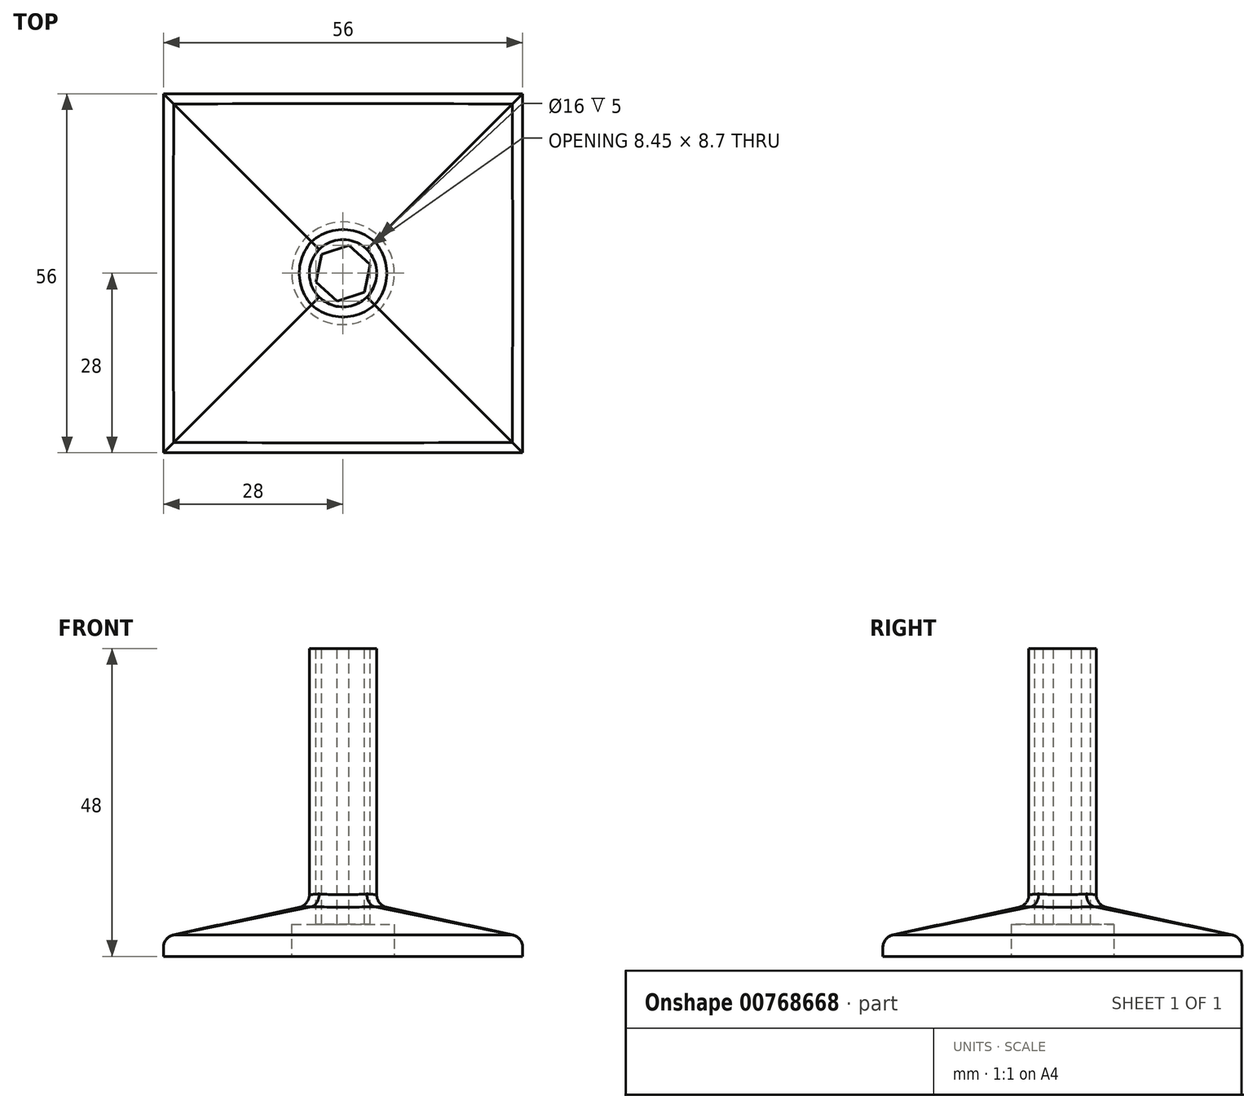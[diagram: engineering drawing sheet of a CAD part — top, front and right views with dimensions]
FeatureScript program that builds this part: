
annotation { "Feature Type Name" : "Feature", "Feature Type Description" : "" }
export const myFeature = defineFeature(function(context is Context, id is Id, definition is map)
    precondition{}
    {
        {
            var Q0;
            Q0=qCreatedBy(makeId("Top.planeOp"),FACE);
            cPlane(context, id + "F0", {"entities" : qUnion([Q0]), "cplaneType" : CPlaneType.OFFSET, "offset" : 8 * mm, "width" : 150 * mm, "height" : 150 * mm});
        }
        {
            var Q0;
            Q0=qCreatedBy(makeId("Top.planeOp"),FACE);
            var sketch = newSketch(context, id + "F1", { "sketchPlane" : qUnion([Q0])});
            skLineSegment(sketch, "E0.bottom", {"start": v(-28, 28) * mm, "end": v(28, 28) * mm});
            skLineSegment(sketch, "E0.top", {"start": v(-28, -28) * mm, "end": v(28, -28) * mm});
            skLineSegment(sketch, "E0.left", {"start": v(-28, 28) * mm, "end": v(-28, -28) * mm});
            skLineSegment(sketch, "E0.right", {"start": v(28, 28) * mm, "end": v(28, -28) * mm});
            skSolve(sketch);
        }
        {
            var Q0;
            Q0=makeQuery(id+"F1.imprint","IMPRINT",FACE,{"disambiguationData":[TD([[makeQuery(id+"F1.imprint","IMPRINT",EDGE,{"derivedFrom":sQuery(id+"F1.wireOp",EDGE,"E0.bottom")}),-1.0]])]});
            extrude(context, id + "F2", {"entities" : qUnion([Q0]), "depth" : 3 * mm, "offsetDistance" : 25 * mm});
        }
        {
            var Q0;
            Q0=qCreatedBy(id+"F0.planeOp",FACE);
            var sketch = newSketch(context, id + "F3", { "sketchPlane" : qUnion([Q0])});
            skCircle(sketch, "E1", {"center": v(0, 0) * mm, "radius": 5.25 * mm});
            skSolve(sketch);
        }
        {
            var Q0;
            Q0=makeQuery(id+"F3.imprint","IMPRINT",FACE,{"disambiguationData":[TD([[makeQuery(id+"F3.imprint","IMPRINT",EDGE,{"derivedFrom":sQuery(id+"F3.wireOp",EDGE,"E1")}),1.0]])]});
            extrude(context, id + "F4", {"entities" : qUnion([Q0]), "operationType" : NewBodyOperationType.ADD, "depth" : 40 * mm, "offsetDistance" : 25 * mm});
        }
        {
            var Q0;
            Q0=makeQuery(id+"F3.imprint","IMPRINT",FACE,{"disambiguationData":[TD([[makeQuery(id+"F3.imprint","IMPRINT",EDGE,{"derivedFrom":sQuery(id+"F3.wireOp",EDGE,"E1")}),1.0]])]});
            var Q1;
            Q1=makeQuery(id+"F2.opExtrude","CAP_FACE",FACE,{"disambiguationData":[OSD([sQuery(id+"F1.wireOp",EDGE,"E0.bottom"),sQuery(id+"F1.wireOp",EDGE,"E0.top"),sQuery(id+"F1.wireOp",EDGE,"E0.left"),sQuery(id+"F1.wireOp",EDGE,"E0.right")])],"isStart":false});
            loft(context, id + "F5", {"sheetProfilesArray" : [{ "sheetProfileEntities" : qUnion([Q0]) }, { "sheetProfileEntities" : qUnion([Q1]) }]});
        }
        {
            var Q0;
            Q0=makeQuery(id+"F2.opExtrude","CAP_FACE",FACE,{"disambiguationData":[OSD([sQuery(id+"F1.wireOp",EDGE,"E0.bottom"),sQuery(id+"F1.wireOp",EDGE,"E0.top"),sQuery(id+"F1.wireOp",EDGE,"E0.left"),sQuery(id+"F1.wireOp",EDGE,"E0.right")])],"isStart":true});
            var sketch = newSketch(context, id + "F6", { "sketchPlane" : qUnion([Q0])});
            skCircle(sketch, "E2", {"center": v(0, 0) * mm, "radius": 8 * mm});
            skSolve(sketch);
        }
        {
            var Q0;
            Q0=makeQuery(id+"F4.opExtrude","CAP_FACE",FACE,{"disambiguationData":[OSD([sQuery(id+"F3.wireOp",EDGE,"E1")])],"isStart":false});
            var sketch = newSketch(context, id + "F7", { "sketchPlane" : qUnion([Q0])});
            skCircle(sketch, "E3.cCircle", {"center": v(0, 0) * mm, "radius": 3.85 * mm, "construction": true});
            skLineSegment(sketch, "E3.0", {"start": v(4.23, 1.38) * mm, "end": v(3.3, -2.97) * mm});
            skLineSegment(sketch, "E3.1", {"start": v(3.3, -2.97) * mm, "end": v(-0.92, -4.35) * mm});
            skLineSegment(sketch, "E3.2", {"start": v(-0.92, -4.35) * mm, "end": v(-4.23, -1.38) * mm});
            skLineSegment(sketch, "E3.3", {"start": v(-4.23, -1.38) * mm, "end": v(-3.3, 2.97) * mm});
            skLineSegment(sketch, "E3.4", {"start": v(-3.3, 2.97) * mm, "end": v(0.92, 4.35) * mm});
            skLineSegment(sketch, "E3.5", {"start": v(0.92, 4.35) * mm, "end": v(4.23, 1.38) * mm});
            skPoint(sketch, "E3.0.midPoint", {"position": v(3.77, -0.8) * mm});
            skSolve(sketch);
        }
        {
            var Q0;
            Q0 = qSketchRegion(id + "F6", true);
            extrude(context, id + "F8", {"entities" : qUnion([Q0]), "operationType" : NewBodyOperationType.REMOVE, "oppositeDirection" : true, "depth" : 5 * mm, "offsetDistance" : 25 * mm});
        }
        {
            var Q0;
            Q0=makeQuery(id+"F7.imprint","IMPRINT",FACE,{"disambiguationData":[TD([[makeQuery(id+"F7.imprint","IMPRINT",EDGE,{"derivedFrom":sQuery(id+"F7.wireOp",EDGE,"E3.0")}),-1.0]])]});
            var Q1;
            Q1=makeQuery(id+"F2.opExtrude","CAP_FACE",FACE,{"disambiguationData":[OSD([sQuery(id+"F1.wireOp",EDGE,"E0.bottom"),sQuery(id+"F1.wireOp",EDGE,"E0.top"),sQuery(id+"F1.wireOp",EDGE,"E0.left"),sQuery(id+"F1.wireOp",EDGE,"E0.right")])],"isStart":true});
            extrude(context, id + "F9", {"entities" : qUnion([Q0]), "operationType" : NewBodyOperationType.REMOVE, "endBound" : BoundingType.THROUGH_ALL, "oppositeDirection" : true, "depth" : 25 * mm, "endBoundEntityFace" : qUnion([Q1]), "offsetDistance" : 25 * mm});
        }
        {
            var Q0;
            Q0=makeQuery(id+"F4.opExtrude","SWEPT_BODY",BODY,{"disambiguationData":[OSD([sQuery(id+"F3.wireOp",EDGE,"E1")])]});
            var Q1;
            Q1=makeQuery(id+"F5.opLoft","SWEPT_BODY",BODY,{"disambiguationData":[OSD([sQuery(id+"F1.wireOp",EDGE,"E0.bottom"),sQuery(id+"F1.wireOp",EDGE,"E0.top"),sQuery(id+"F1.wireOp",EDGE,"E0.left"),sQuery(id+"F1.wireOp",EDGE,"E0.right"),makeQuery(id+"F3.imprint","IMPRINT",FACE,{"disambiguationData":[TD([[makeQuery(id+"F3.imprint","IMPRINT",EDGE,{"derivedFrom":sQuery(id+"F3.wireOp",EDGE,"E1")}),1.0]])]})])]});
            var Q2;
            Q2=makeQuery(id+"F2.opExtrude","SWEPT_BODY",BODY,{"disambiguationData":[OSD([sQuery(id+"F1.wireOp",EDGE,"E0.bottom"),sQuery(id+"F1.wireOp",EDGE,"E0.top"),sQuery(id+"F1.wireOp",EDGE,"E0.left"),sQuery(id+"F1.wireOp",EDGE,"E0.right")])]});
            booleanBodies(context, id + "F10", {"operationType" : BooleanOperationType.UNION, "tools" : qUnion([Q0, Q1, Q2])});
        }
        {
            var Q0;
            {var subQ0=sQuery(id+"F1.wireOp",EDGE,"E0.left");Q0=makeQuery(id+"F10.opBoolean","MERGE",EDGE,{"derivedFrom":[makeQuery(id+"F2.opExtrude","CAP_EDGE",EDGE,{"disambiguationData":[OSD([subQ0])],"isStart":false}),makeQuery(id+"F5.opLoft","MID_CAP_EDGE",EDGE,{"disambiguationData":[OSD([sQuery(id+"F1.wireOp",EDGE,"E0.bottom"),sQuery(id+"F1.wireOp",EDGE,"E0.top"),subQ0])],"capPos":1.0})]});}
            var Q1;
            {var subQ0=sQuery(id+"F1.wireOp",EDGE,"E0.top");Q1=makeQuery(id+"F10.opBoolean","MERGE",EDGE,{"derivedFrom":[makeQuery(id+"F2.opExtrude","CAP_EDGE",EDGE,{"disambiguationData":[OSD([subQ0])],"isStart":false}),makeQuery(id+"F5.opLoft","MID_CAP_EDGE",EDGE,{"disambiguationData":[OSD([subQ0,sQuery(id+"F1.wireOp",EDGE,"E0.left"),sQuery(id+"F1.wireOp",EDGE,"E0.right")])],"capPos":1.0})]});}
            var Q2;
            {var subQ0=sQuery(id+"F1.wireOp",EDGE,"E0.right");Q2=makeQuery(id+"F10.opBoolean","MERGE",EDGE,{"derivedFrom":[makeQuery(id+"F2.opExtrude","CAP_EDGE",EDGE,{"disambiguationData":[OSD([subQ0])],"isStart":false}),makeQuery(id+"F5.opLoft","MID_CAP_EDGE",EDGE,{"disambiguationData":[OSD([sQuery(id+"F1.wireOp",EDGE,"E0.bottom"),sQuery(id+"F1.wireOp",EDGE,"E0.top"),subQ0])],"capPos":1.0})]});}
            var Q3;
            {var subQ0=sQuery(id+"F1.wireOp",EDGE,"E0.bottom");Q3=makeQuery(id+"F10.opBoolean","MERGE",EDGE,{"derivedFrom":[makeQuery(id+"F2.opExtrude","CAP_EDGE",EDGE,{"disambiguationData":[OSD([subQ0])],"isStart":false}),makeQuery(id+"F5.opLoft","MID_CAP_EDGE",EDGE,{"disambiguationData":[OSD([subQ0,sQuery(id+"F1.wireOp",EDGE,"E0.left"),sQuery(id+"F1.wireOp",EDGE,"E0.right")])],"capPos":1.0})]});}
            var Q4;
            {var subQ0=sQuery(id+"F3.wireOp",EDGE,"E1");Q4=makeQuery(id+"F10.opBoolean","MERGE",EDGE,{"derivedFrom":[makeQuery(id+"F4.opExtrude","CAP_EDGE",EDGE,{"disambiguationData":[OSD([subQ0])],"isStart":true}),makeQuery(id+"F5.opLoft","MID_CAP_EDGE",EDGE,{"disambiguationData":[OSD([sQuery(id+"F1.wireOp",EDGE,"E0.bottom"),sQuery(id+"F1.wireOp",EDGE,"E0.left"),subQ0])],"capPos":0.0})]});}
            fillet(context, id + "F11", {"entities" : qUnion([Q0, Q1, Q2, Q3, Q4]), "radius" : 2 * mm, "tangentPropagation" : true, "allowEdgeOverflow" : false});
        }
    });
